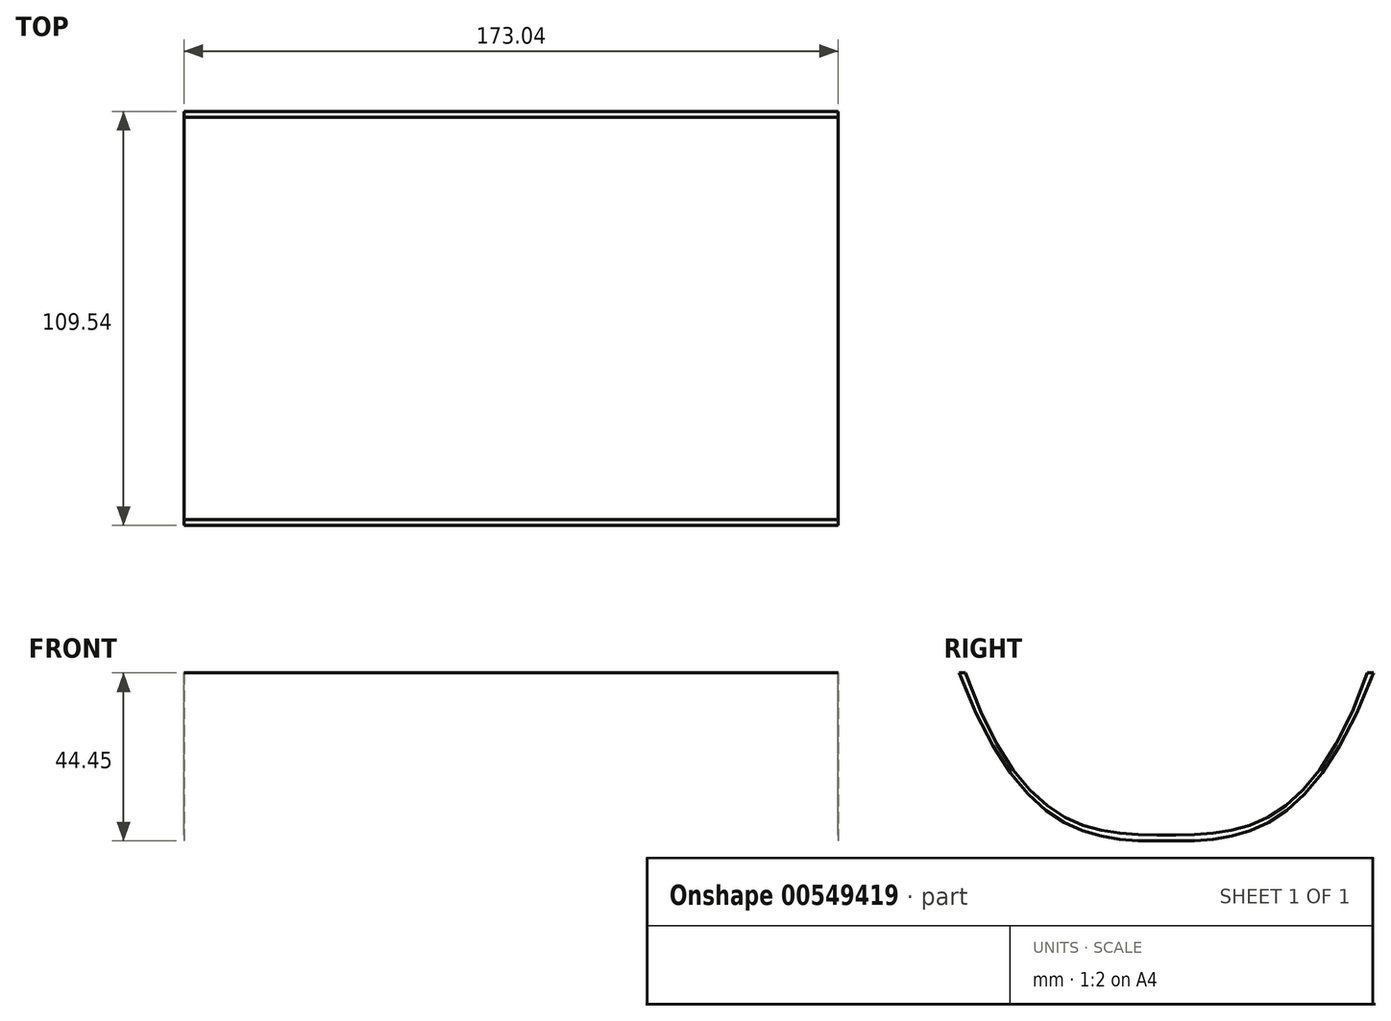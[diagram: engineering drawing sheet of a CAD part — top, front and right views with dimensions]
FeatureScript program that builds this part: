
annotation { "Feature Type Name" : "Feature", "Feature Type Description" : "" }
export const myFeature = defineFeature(function(context is Context, id is Id, definition is map)
    precondition{}
    {
        {
            var Q0;
            Q0=qCreatedBy(makeId("Right.planeOp"),FACE);
            var sketch = newSketch(context, id + "F0", { "sketchPlane" : qUnion([Q0])});
            skFitSpline(sketch, "E0", {"points": [v(-54.77, 0) * mm, v(0, -44.45) * mm, v(54.77, 0) * mm], "startDerivative": vector(100.81, -266.7) * mm, "endDerivative": vector(100.81, 266.7) * mm});
            skFitSpline(sketch, "E1", {"points": [v(-53.18, 0) * mm, v(0, -42.86) * mm, v(53.18, 0) * mm], "startDerivative": vector(91.29, -257.18) * mm, "endDerivative": vector(91.29, 257.18) * mm});
            skLineSegment(sketch, "E2", {"start": v(-54.77, 0) * mm, "end": v(-53.18, 0) * mm});
            skLineSegment(sketch, "E3", {"start": v(54.77, 0) * mm, "end": v(53.18, 0) * mm});
            skSolve(sketch);
        }
        {
            var Q0;
            Q0=makeQuery(id+"F0.imprint","IMPRINT",FACE,{"disambiguationData":[TD([[makeQuery(id+"F0.imprint","IMPRINT",EDGE,{"derivedFrom":sQuery(id+"F0.wireOp",EDGE,"E0")}),1.0]])]});
            extrude(context, id + "F1", {"entities" : qUnion([Q0]), "endBound" : BoundingType.SYMMETRIC, "depth" : 173.04 * mm, "offsetDistance" : 25.4 * mm});
        }
    });
